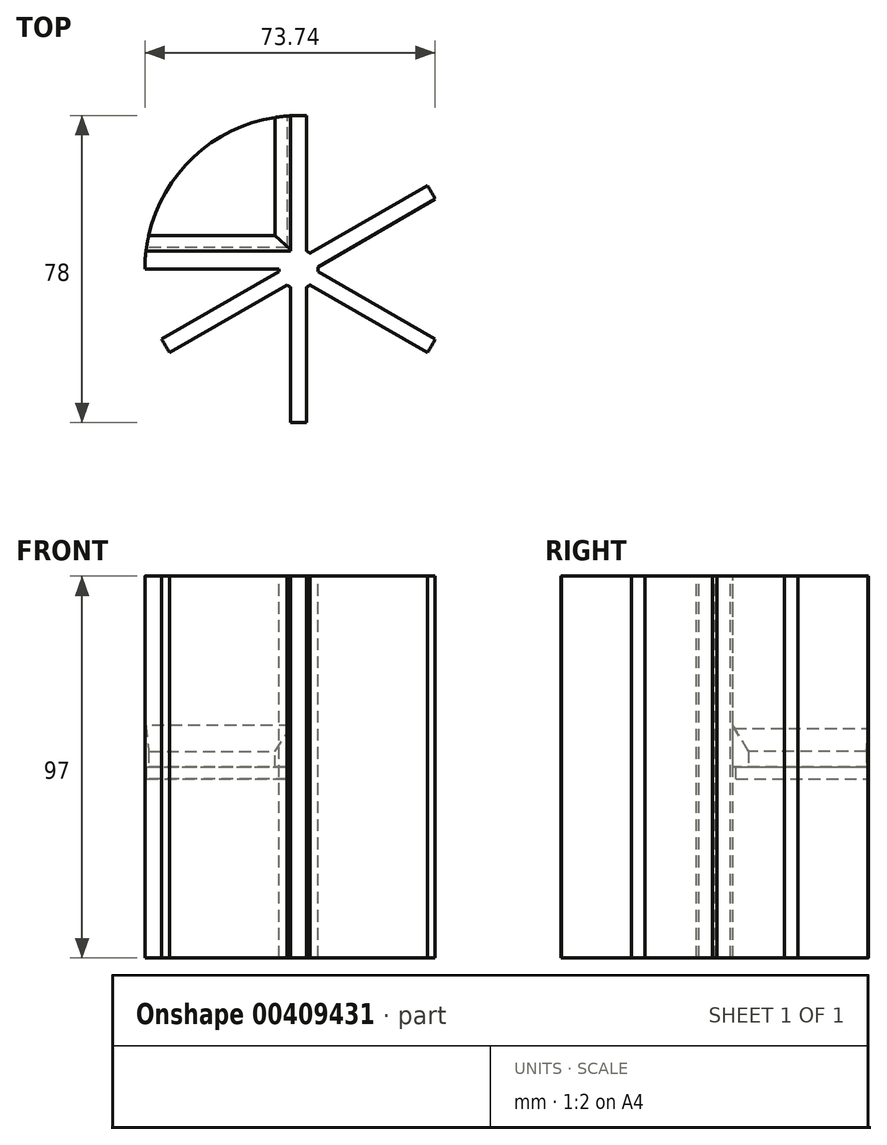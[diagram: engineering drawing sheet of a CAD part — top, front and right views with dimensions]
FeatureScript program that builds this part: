
annotation { "Feature Type Name" : "Feature", "Feature Type Description" : "" }
export const myFeature = defineFeature(function(context is Context, id is Id, definition is map)
    precondition{}
    {
        {
            var Q0;
            Q0=qCreatedBy(makeId("Top.planeOp"),FACE);
            var sketch = newSketch(context, id + "F0", { "sketchPlane" : qUnion([Q0])});
            skArc(sketch, "E0", {"start": v(2, 38.95) * mm, "mid": v(0, 39) * mm, "end": v(-2, 38.95) * mm});
            skLineSegment(sketch, "E1.0", {"start": v(-2, 4.58) * mm, "end": v(-2, 38.95) * mm});
            skLineSegment(sketch, "E2.trimOffspring", {"start": v(2, 4.58) * mm, "end": v(2, 38.95) * mm});
            skLineSegment(sketch, "E3.0", {"start": v(4.97, 0.56) * mm, "end": v(34.73, 17.74) * mm});
            skLineSegment(sketch, "E4.trimOffspring", {"start": v(2.97, 4.02) * mm, "end": v(32.73, 21.2) * mm});
            skArc(sketch, "E5.trimOffspring", {"start": v(34.73, 17.74) * mm, "mid": v(33.77, 19.5) * mm, "end": v(32.73, 21.2) * mm});
            skLineSegment(sketch, "E6.1.0", {"start": v(-2.97, -4.02) * mm, "end": v(-32.73, -21.2) * mm});
            skArc(sketch, "E6.1.1", {"start": v(-34.73, -17.74) * mm, "mid": v(-33.77, -19.5) * mm, "end": v(-32.73, -21.2) * mm});
            skLineSegment(sketch, "E6.1.2", {"start": v(-4.97, -0.56) * mm, "end": v(-34.73, -17.74) * mm});
            skArc(sketch, "E6.1.5", {"start": v(-32.73, 21.2) * mm, "mid": v(-33.77, 19.5) * mm, "end": v(-34.73, 17.74) * mm});
            skLineSegment(sketch, "E6.2.0", {"start": v(4.97, -0.56) * mm, "end": v(34.73, -17.74) * mm});
            skArc(sketch, "E6.2.1", {"start": v(32.73, -21.2) * mm, "mid": v(33.77, -19.5) * mm, "end": v(34.73, -17.74) * mm});
            skLineSegment(sketch, "E6.2.2", {"start": v(2.97, -4.02) * mm, "end": v(32.73, -21.2) * mm});
            skLineSegment(sketch, "E6.2.3", {"start": v(2, -4.58) * mm, "end": v(2, -38.95) * mm});
            skLineSegment(sketch, "E6.2.4", {"start": v(-2, -4.58) * mm, "end": v(-2, -38.95) * mm});
            skArc(sketch, "E6.2.5", {"start": v(-2, -38.95) * mm, "mid": v(0, -39) * mm, "end": v(2, -38.95) * mm});
            skArc(sketch, "E7.trimOffspring", {"start": v(2.97, 4.02) * mm, "mid": v(2.5, 4.33) * mm, "end": v(2, 4.58) * mm});
            skArc(sketch, "E8.trimOffspring", {"start": v(4.97, -0.56) * mm, "mid": v(5, 0) * mm, "end": v(4.97, 0.56) * mm});
            skArc(sketch, "E9.trimOffspring", {"start": v(2, -4.58) * mm, "mid": v(2.5, -4.33) * mm, "end": v(2.97, -4.02) * mm});
            skArc(sketch, "E10.trimOffspring", {"start": v(-2.97, -4.02) * mm, "mid": v(-2.5, -4.33) * mm, "end": v(-2, -4.58) * mm});
            skArc(sketch, "E11.trimOffspring", {"start": v(-5, 0) * mm, "mid": v(-5, -0.28) * mm, "end": v(-4.97, -0.56) * mm});
            skCircle(sketch, "E12", {"center": v(0, 0) * mm, "radius": 39 * mm, "construction": true});
            skLineSegment(sketch, "E13", {"start": v(-4.97, 0) * mm, "end": v(-39, 0) * mm});
            skPoint(sketch, "E13.startSnap0", {"position": v(-5, 0) * mm});
            skLineSegment(sketch, "E14", {"start": v(-2, 4.58) * mm, "end": v(-38.73, 4.58) * mm});
            skArc(sketch, "E15", {"start": v(-38.73, 4.58) * mm, "mid": v(-38.97, 2.3) * mm, "end": v(-39, 0) * mm});
            skSolve(sketch);
        }
        {
            var Q0;
            Q0 = qSketchRegion(id + "F0", true);
            extrude(context, id + "F1", {"entities" : qUnion([Q0]), "oppositeDirection" : true, "depth" : 97 * mm, "offsetDistance" : 25 * mm});
        }
        {
            var Q0;
            Q0=makeQuery(id+"F1.opExtrude","SWEPT_FACE",FACE,{"disambiguationData":[OSD([sQuery(id+"F0.wireOp",EDGE,"E14")])]});
            var sketch = newSketch(context, id + "F2", { "sketchPlane" : qUnion([Q0])});
            skLineSegment(sketch, "E16.bottom", {"start": v(38.73, -48.5) * mm, "end": v(2, -48.5) * mm});
            skLineSegment(sketch, "E16.top", {"start": v(38.73, -44.5) * mm, "end": v(2, -44.5) * mm});
            skLineSegment(sketch, "E16.left", {"start": v(38.73, -48.5) * mm, "end": v(38.73, -44.5) * mm});
            skLineSegment(sketch, "E16.right", {"start": v(2, -48.5) * mm, "end": v(2, -44.5) * mm});
            skSolve(sketch);
        }
        {
            var Q0;
            Q0 = qSketchRegion(id + "F2", true);
            extrude(context, id + "F3", {"entities" : qUnion([Q0]), "operationType" : NewBodyOperationType.ADD, "depth" : 4 * mm, "offsetDistance" : 25 * mm});
        }
        {
            var Q0;
            Q0=makeQuery(id+"F3.opExtrude","SWEPT_FACE",FACE,{"disambiguationData":[OSD([sQuery(id+"F2.wireOp",EDGE,"E16.left")])]});
            var sketch = newSketch(context, id + "F4", { "sketchPlane" : qUnion([Q0])});
            skLineSegment(sketch, "E17", {"start": v(-8.58, -44.5) * mm, "end": v(-4.58, -37.93) * mm});
            skLineSegment(sketch, "E18", {"start": v(-4.58, -37.93) * mm, "end": v(-4.58, -44.5) * mm});
            skLineSegment(sketch, "E19", {"start": v(-4.58, -44.5) * mm, "end": v(-8.58, -44.5) * mm});
            skSolve(sketch);
        }
        {
            var Q0;
            Q0 = qSketchRegion(id + "F4", true);
            extrude(context, id + "F5", {"entities" : qUnion([Q0]), "operationType" : NewBodyOperationType.ADD, "oppositeDirection" : true, "depth" : 36.75 * mm, "offsetDistance" : 25 * mm});
        }
        {
            var Q0;
            Q0=makeQuery(id+"F1.opExtrude","SWEPT_FACE",FACE,{"disambiguationData":[OSD([sQuery(id+"F0.wireOp",EDGE,"E1.0")])]});
            var sketch = newSketch(context, id + "F6", { "sketchPlane" : qUnion([Q0])});
            skLineSegment(sketch, "E20", {"start": v(-8.58, -48.5) * mm, "end": v(-38.95, -48.5) * mm});
            skLineSegment(sketch, "E21", {"start": v(-38.95, -48.5) * mm, "end": v(-38.95, -44.5) * mm});
            skLineSegment(sketch, "E22", {"start": v(-38.95, -44.5) * mm, "end": v(-8.58, -44.5) * mm});
            skLineSegment(sketch, "E23", {"start": v(-8.58, -44.5) * mm, "end": v(-8.58, -48.5) * mm});
            skSolve(sketch);
        }
        {
            var Q0;
            Q0 = qSketchRegion(id + "F6", true);
            extrude(context, id + "F7", {"entities" : qUnion([Q0]), "operationType" : NewBodyOperationType.ADD, "depth" : 4 * mm, "offsetDistance" : 25 * mm});
        }
        {
            var Q0;
            Q0=makeQuery(id+"F7.opExtrude","SWEPT_FACE",FACE,{"disambiguationData":[OSD([sQuery(id+"F6.wireOp",EDGE,"E21")])]});
            var sketch = newSketch(context, id + "F8", { "sketchPlane" : qUnion([Q0])});
            skLineSegment(sketch, "E24", {"start": v(6, -44.5) * mm, "end": v(2, -44.5) * mm});
            skLineSegment(sketch, "E25", {"start": v(2, -44.5) * mm, "end": v(2, -38.66) * mm});
            skLineSegment(sketch, "E26", {"start": v(2, -38.66) * mm, "end": v(6, -44.5) * mm});
            skSolve(sketch);
        }
        {
            var Q0;
            Q0 = qSketchRegion(id + "F8", true);
            extrude(context, id + "F9", {"entities" : qUnion([Q0]), "operationType" : NewBodyOperationType.ADD, "oppositeDirection" : true, "depth" : 36.75 * mm, "offsetDistance" : 25 * mm});
        }
        {
            var Q0;
            Q0=makeQuery(id+"F7.boolean.opBoolean","MERGE",FACE,{"derivedFrom":[makeQuery(id+"F3.opExtrude","SWEPT_FACE",FACE,{"disambiguationData":[OSD([sQuery(id+"F2.wireOp",EDGE,"E16.bottom")])]}),makeQuery(id+"F7.opExtrude","SWEPT_FACE",FACE,{"disambiguationData":[OSD([sQuery(id+"F6.wireOp",EDGE,"E20")])]})]});
            var sketch = newSketch(context, id + "F10", { "sketchPlane" : qUnion([Q0])});
            skArc(sketch, "E27", {"start": v(-38.73, -4.58) * mm, "mid": v(-26.65, -28.48) * mm, "end": v(-2, -38.95) * mm});
            skLineSegment(sketch, "E28", {"start": v(-2, -38.95) * mm, "end": v(-40.09, -48.13) * mm});
            skLineSegment(sketch, "E29", {"start": v(-40.09, -48.13) * mm, "end": v(-38.73, -4.58) * mm});
            skSolve(sketch);
        }
        {
            var Q0;
            Q0 = qSketchRegion(id + "F10", true);
            extrude(context, id + "F11", {"entities" : qUnion([Q0]), "operationType" : NewBodyOperationType.REMOVE, "oppositeDirection" : true, "depth" : 100 * mm, "offsetDistance" : 25 * mm, "symmetric" : true});
        }
        {
            var Q0;
            Q0=makeQuery(id+"F7.boolean.opBoolean","MERGE",FACE,{"derivedFrom":[makeQuery(id+"F3.opExtrude","SWEPT_FACE",FACE,{"disambiguationData":[OSD([sQuery(id+"F2.wireOp",EDGE,"E16.bottom")])]}),makeQuery(id+"F7.opExtrude","SWEPT_FACE",FACE,{"disambiguationData":[OSD([sQuery(id+"F6.wireOp",EDGE,"E20")])]})]});
            var sketch = newSketch(context, id + "F12", { "sketchPlane" : qUnion([Q0])});
            skArc(sketch, "E30", {"start": v(-38.62, -5.44) * mm, "mid": v(-26.61, -28.5) * mm, "end": v(-2.77, -38.9) * mm});
            skLineSegment(sketch, "E31", {"start": v(-2.77, -5.44) * mm, "end": v(-2.77, -38.9) * mm});
            skLineSegment(sketch, "E32", {"start": v(-2.77, -5.44) * mm, "end": v(-38.62, -5.44) * mm});
            skSolve(sketch);
        }
        {
            var Q0;
            Q0 = qSketchRegion(id + "F12", true);
            extrude(context, id + "F13", {"entities" : qUnion([Q0]), "depth" : 3 * mm, "offsetDistance" : 25 * mm});
        }
    });
